FCSTD DOCUMENT  (FreeCAD 0.16R6706 (Git))
Label: PCB_Outline
License: All rights reserved
LicenseURL: http://de.wikipedia.org/wiki/Alle_Rechte_vorbehalten
objects: Sketcher::SketchObject×1
note: 1 computed .brp shape members not serialized (recipe doc carries the construction recipe); baked Part::Feature solids carry a one-line shape summary decoded from their .brp

FEATURE [Sketcher::SketchObject] Sketch
  sketch-geometry (16):
    g0: Circle CenterX=0 CenterY=0 CenterZ=0 NormalX=0 NormalY=0 NormalZ=1 Radius=15
    g1: ArcOfCircle CenterX=0 CenterY=0 CenterZ=0 NormalX=0 NormalY=0 NormalZ=1 Radius=55 StartAngle=1.67096 EndAngle=3.56502
    g2: LineSegment StartX=-5.5 StartY=54.7243 StartZ=0 EndX=-5.5 EndY=195 EndZ=0
    g3: LineSegment StartX=5.5 StartY=195 StartZ=0 EndX=5.5 EndY=54.7243 EndZ=0
    g4: LineSegment [constr] StartX=0 StartY=0 StartZ=0 EndX=168.875 EndY=-97.5 EndZ=0
    g5: LineSegment [constr] StartX=0 StartY=0 StartZ=0 EndX=-168.875 EndY=-97.5 EndZ=0
    g6: LineSegment [constr] StartX=0 StartY=0 StartZ=0 EndX=0 EndY=195 EndZ=0
    g7: LineSegment StartX=50.1426 StartY=-22.599 StartZ=0 EndX=171.625 EndY=-92.7369 EndZ=0
    g8: LineSegment StartX=44.6426 StartY=-32.1253 StartZ=0 EndX=166.125 EndY=-102.263 EndZ=0
    g9: LineSegment StartX=171.625 StartY=-92.7369 StartZ=0 EndX=166.125 EndY=-102.263 EndZ=0
    g10: ArcOfCircle CenterX=0 CenterY=0 CenterZ=0 NormalX=0 NormalY=0 NormalZ=1 Radius=55 StartAngle=5.85975 EndAngle=7.75381
    g11: LineSegment StartX=-5.5 StartY=195 StartZ=0 EndX=5.5 EndY=195 EndZ=0
    g12: LineSegment StartX=-50.1426 StartY=-22.599 StartZ=0 EndX=-171.625 EndY=-92.7369 EndZ=0
    g13: LineSegment StartX=-44.6426 StartY=-32.1253 StartZ=0 EndX=-166.125 EndY=-102.263 EndZ=0
    g14: LineSegment StartX=-171.625 StartY=-92.7369 StartZ=0 EndX=-166.125 EndY=-102.263 EndZ=0
    g15: ArcOfCircle CenterX=0 CenterY=0 CenterZ=0 NormalX=0 NormalY=0 NormalZ=1 Radius=55 StartAngle=3.76536 EndAngle=5.65942
  constraints (47):
    c: Radius(g0) = 15
    c: Radius(g1) = 55
    c: Vertical(g2)
    c: Vertical(g3)
    c: Coincident(g1,g2)
    c: Coincident(g10,g3)
    c: DistanceX(g2,g3) = 11
    c: Coincident(g1,g-1)
    c: Symmetric(g2,g3,g-2)
    c: Coincident(g4,g-1)
    c: Coincident(g5,g-1)
    c: Coincident(g6,g-1)
    c: Vertical(g6)
    c: Angle(g4,g6) = 2.0944
    c: Angle(g6,g5) = 2.0944
    c: Coincident(g0,g-1)
    c: Parallel(g7,g4)
    c: Parallel(g4,g8)
    c: Coincident(g9,g7)
    c: Coincident(g9,g8)
    c: PointOnObject(g4,g9)
    c: Perpendicular(g9,g4)
    c: Distance(g9) = 11
    c: Symmetric(g7,g8,g4)
    c: Distance(g-1,g4) = 195
    c: Equal(g1,g10)
    c: Coincident(g10,g7)
    c: Coincident(g1,g10)
    c: Coincident(g15,g8)
    c: Distance(g-1,g5) = 195
    c: Coincident(g11,g2)
    c: Coincident(g11,g3)
    c: PointOnObject(g6,g11)
    c: DistanceY(g-1,g6) = 195
    c: PointOnObject(g13,g1)
    c: Coincident(g14,g12)
    c: Coincident(g14,g13)
    c: Parallel(g12,g5)
    c: Parallel(g13,g5)
    c: PointOnObject(g5,g14)
    c: Perpendicular(g5,g14)
    c: Symmetric(g13,g12,g5)
    c: Distance(g13,g12) = 11
    c: Equal(g1,g15)
    c: Coincident(g1,g12)
    c: Coincident(g1,g15)
    c: PointOnObject(g15,g13)
